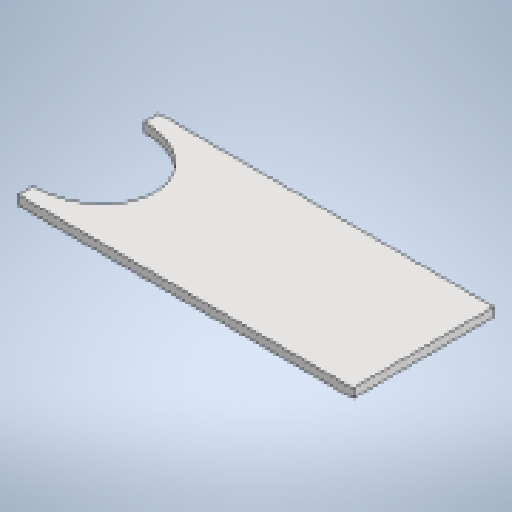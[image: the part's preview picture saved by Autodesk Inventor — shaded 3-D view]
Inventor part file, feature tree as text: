
AUTODESK INVENTOR PART (.ipt)
format: ipt  version: 2025.1 (Build 291241020, 241B)  size: 166,400 bytes
history: native  units: mm
features: other x2, sheet_metal_op x1, sketch x1
ambient origin geometry x8: Origin, YZ Plane, XZ Plane, XY Plane, X Axis, Y Axis, Z Axis, Center Point
bodies: Body1 (feature_tree)
feature tree (4):
  sheet_metal_op  "Face1"
  sketch  "Sketch1"  dims[d12=75.0mm d13=63.0mm d14=160.0mm d15=380.0mm d16=10.0mm]
  other  "Plate1"
  other  "Definition1"
